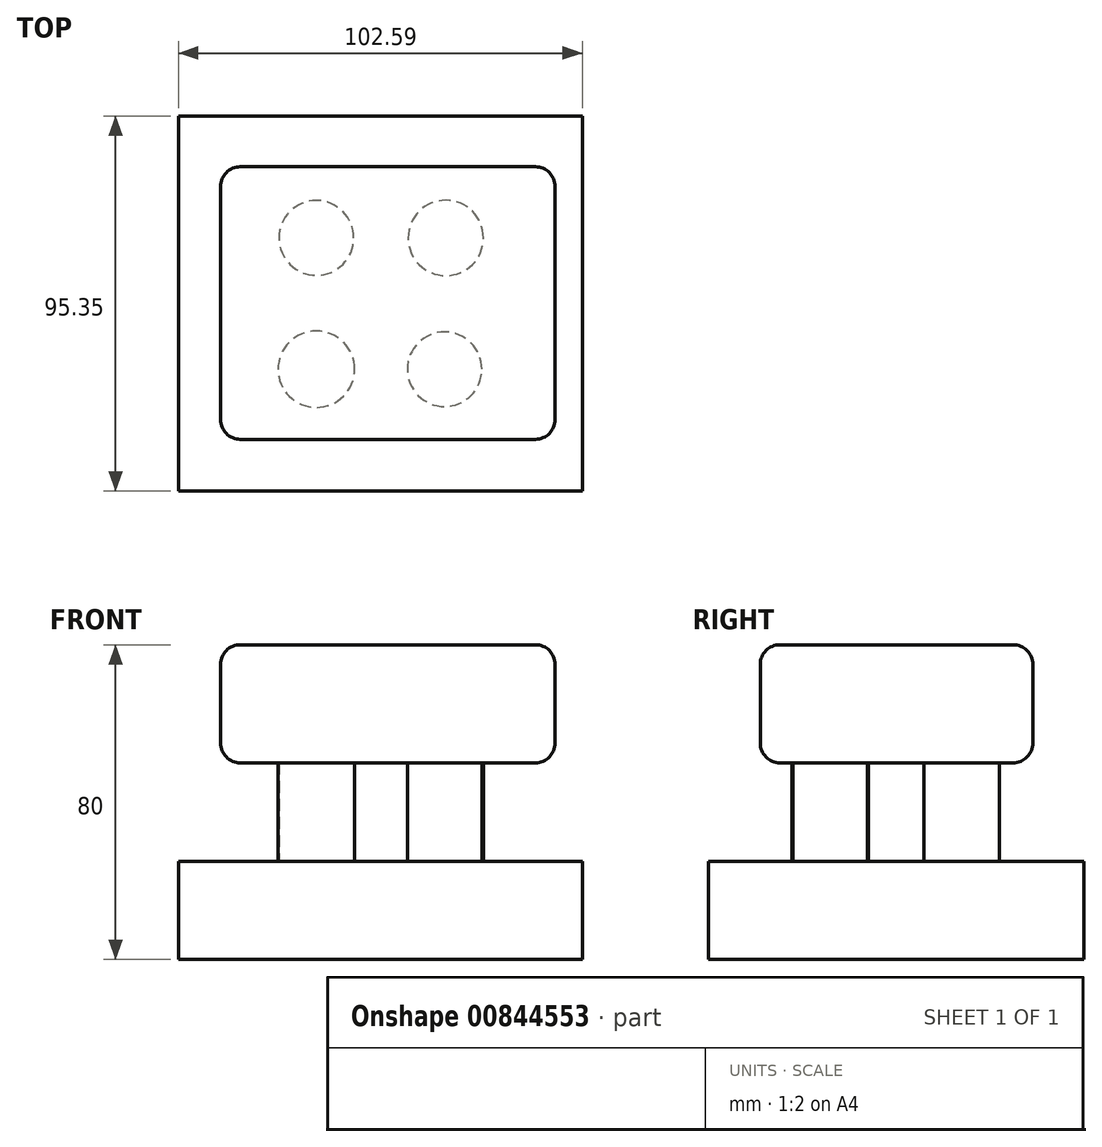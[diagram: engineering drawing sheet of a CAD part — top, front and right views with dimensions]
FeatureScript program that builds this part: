
annotation { "Feature Type Name" : "Feature", "Feature Type Description" : "" }
export const myFeature = defineFeature(function(context is Context, id is Id, definition is map)
    precondition{}
    {
        {
            var Q0;
            Q0=qCreatedBy(makeId("Top.planeOp"),FACE);
            var sketch = newSketch(context, id + "F0", { "sketchPlane" : qUnion([Q0])});
            skLineSegment(sketch, "E0.bottom", {"start": v(49.42, -47.81) * mm, "end": v(-53.17, -47.81) * mm});
            skLineSegment(sketch, "E0.top", {"start": v(49.42, 47.54) * mm, "end": v(-53.17, 47.54) * mm});
            skLineSegment(sketch, "E0.left", {"start": v(49.42, -47.81) * mm, "end": v(49.42, 47.54) * mm});
            skLineSegment(sketch, "E0.right", {"start": v(-53.17, -47.81) * mm, "end": v(-53.17, 47.54) * mm});
            skSolve(sketch);
        }
        {
            var Q0;
            Q0=qSketchRegion(id+"F0",true);
            extrude(context, id + "F1", {"entities" : qUnion([Q0]), "depth" : 25 * mm, "offsetDistance" : 25 * mm});
        }
        {
            var Q0;
            Q0=makeQuery(id+"F1.opExtrude","CAP_FACE",FACE,{"disambiguationData":[OSD([sQuery(id+"F0.wireOp",EDGE,"E0.bottom"),sQuery(id+"F0.wireOp",EDGE,"E0.top"),sQuery(id+"F0.wireOp",EDGE,"E0.left"),sQuery(id+"F0.wireOp",EDGE,"E0.right")])],"isStart":false});
            var sketch = newSketch(context, id + "F2", { "sketchPlane" : qUnion([Q0])});
            skCircle(sketch, "E1", {"center": v(14.72, 16.54) * mm, "radius": 9.57 * mm});
            skCircle(sketch, "E2", {"center": v(-18.17, 16.54) * mm, "radius": 9.52 * mm});
            skCircle(sketch, "E3", {"center": v(-18.17, -16.81) * mm, "radius": 9.72 * mm});
            skCircle(sketch, "E4", {"center": v(14.42, -16.81) * mm, "radius": 9.47 * mm});
            skSolve(sketch);
        }
        {
            var Q0;
            Q0 = qSketchRegion(id + "F2", true);
            extrude(context, id + "F3", {"entities" : qUnion([Q0]), "operationType" : NewBodyOperationType.ADD, "depth" : 25 * mm, "offsetDistance" : 25 * mm});
        }
        {
            var Q0;
            Q0=makeQuery(id+"F3.opExtrude","CAP_FACE",FACE,{"disambiguationData":[OSD([sQuery(id+"F2.wireOp",EDGE,"E2")])],"isStart":false});
            var sketch = newSketch(context, id + "F4", { "sketchPlane" : qUnion([Q0])});
            skLineSegment(sketch, "E5.bottom", {"start": v(42.48, -34.62) * mm, "end": v(-42.48, -34.62) * mm});
            skLineSegment(sketch, "E5.top", {"start": v(42.48, 34.62) * mm, "end": v(-42.48, 34.62) * mm});
            skLineSegment(sketch, "E5.left", {"start": v(42.48, -34.62) * mm, "end": v(42.48, 34.62) * mm});
            skLineSegment(sketch, "E5.right", {"start": v(-42.48, -34.62) * mm, "end": v(-42.48, 34.62) * mm});
            skPoint(sketch, "E5.middle", {"position": v(0, 0) * mm});
            skSolve(sketch);
        }
        {
            var Q0;
            Q0 = qSketchRegion(id + "F4", true);
            extrude(context, id + "F5", {"entities" : qUnion([Q0]), "operationType" : NewBodyOperationType.ADD, "depth" : 30 * mm, "offsetDistance" : 25 * mm});
        }
        {
            var Q0;
            Q0=makeQuery(id+"F5.opExtrude","CAP_EDGE",EDGE,{"disambiguationData":[OSD([sQuery(id+"F4.wireOp",EDGE,"E5.left")])],"isStart":false});
            var Q1;
            Q1=makeQuery(id+"F5.opExtrude","CAP_EDGE",EDGE,{"disambiguationData":[OSD([sQuery(id+"F4.wireOp",EDGE,"E5.bottom")])],"isStart":false});
            var Q2;
            Q2=makeQuery(id+"F5.opExtrude","CAP_EDGE",EDGE,{"disambiguationData":[OSD([sQuery(id+"F4.wireOp",EDGE,"E5.right")])],"isStart":false});
            var Q3;
            Q3=makeQuery(id+"F5.opExtrude","CAP_EDGE",EDGE,{"disambiguationData":[OSD([sQuery(id+"F4.wireOp",EDGE,"E5.top")])],"isStart":false});
            var Q4;
            Q4=makeQuery(id+"F5.opExtrude","SWEPT_EDGE",EDGE,{"disambiguationData":[OSD([sQuery(id+"F4.wireOp",EDGE,"E5.bottom"),sQuery(id+"F4.wireOp",EDGE,"E5.left")])]});
            var Q5;
            Q5=makeQuery(id+"F5.opExtrude","SWEPT_EDGE",EDGE,{"disambiguationData":[OSD([sQuery(id+"F4.wireOp",EDGE,"E5.top"),sQuery(id+"F4.wireOp",EDGE,"E5.left")])]});
            var Q6;
            Q6=makeQuery(id+"F5.opExtrude","SWEPT_EDGE",EDGE,{"disambiguationData":[OSD([sQuery(id+"F4.wireOp",EDGE,"E5.top"),sQuery(id+"F4.wireOp",EDGE,"E5.right")])]});
            var Q7;
            Q7=makeQuery(id+"F5.opExtrude","SWEPT_EDGE",EDGE,{"disambiguationData":[OSD([sQuery(id+"F4.wireOp",EDGE,"E5.bottom"),sQuery(id+"F4.wireOp",EDGE,"E5.right")])]});
            var Q8;
            Q8=makeQuery(id+"F5.opExtrude","CAP_EDGE",EDGE,{"disambiguationData":[OSD([sQuery(id+"F4.wireOp",EDGE,"E5.bottom")])],"isStart":true});
            var Q9;
            Q9=makeQuery(id+"F5.opExtrude","CAP_EDGE",EDGE,{"disambiguationData":[OSD([sQuery(id+"F4.wireOp",EDGE,"E5.right")])],"isStart":true});
            var Q10;
            Q10=makeQuery(id+"F5.opExtrude","CAP_EDGE",EDGE,{"disambiguationData":[OSD([sQuery(id+"F4.wireOp",EDGE,"E5.top")])],"isStart":true});
            var Q11;
            Q11=makeQuery(id+"F5.opExtrude","CAP_EDGE",EDGE,{"disambiguationData":[OSD([sQuery(id+"F4.wireOp",EDGE,"E5.left")])],"isStart":true});
            fillet(context, id + "F6", {"entities" : qUnion([Q0, Q1, Q2, Q3, Q4, Q5, Q6, Q7, Q8, Q9, Q10, Q11]), "radius" : 5 * mm, "tangentPropagation" : true, "allowEdgeOverflow" : false});
        }
    });
